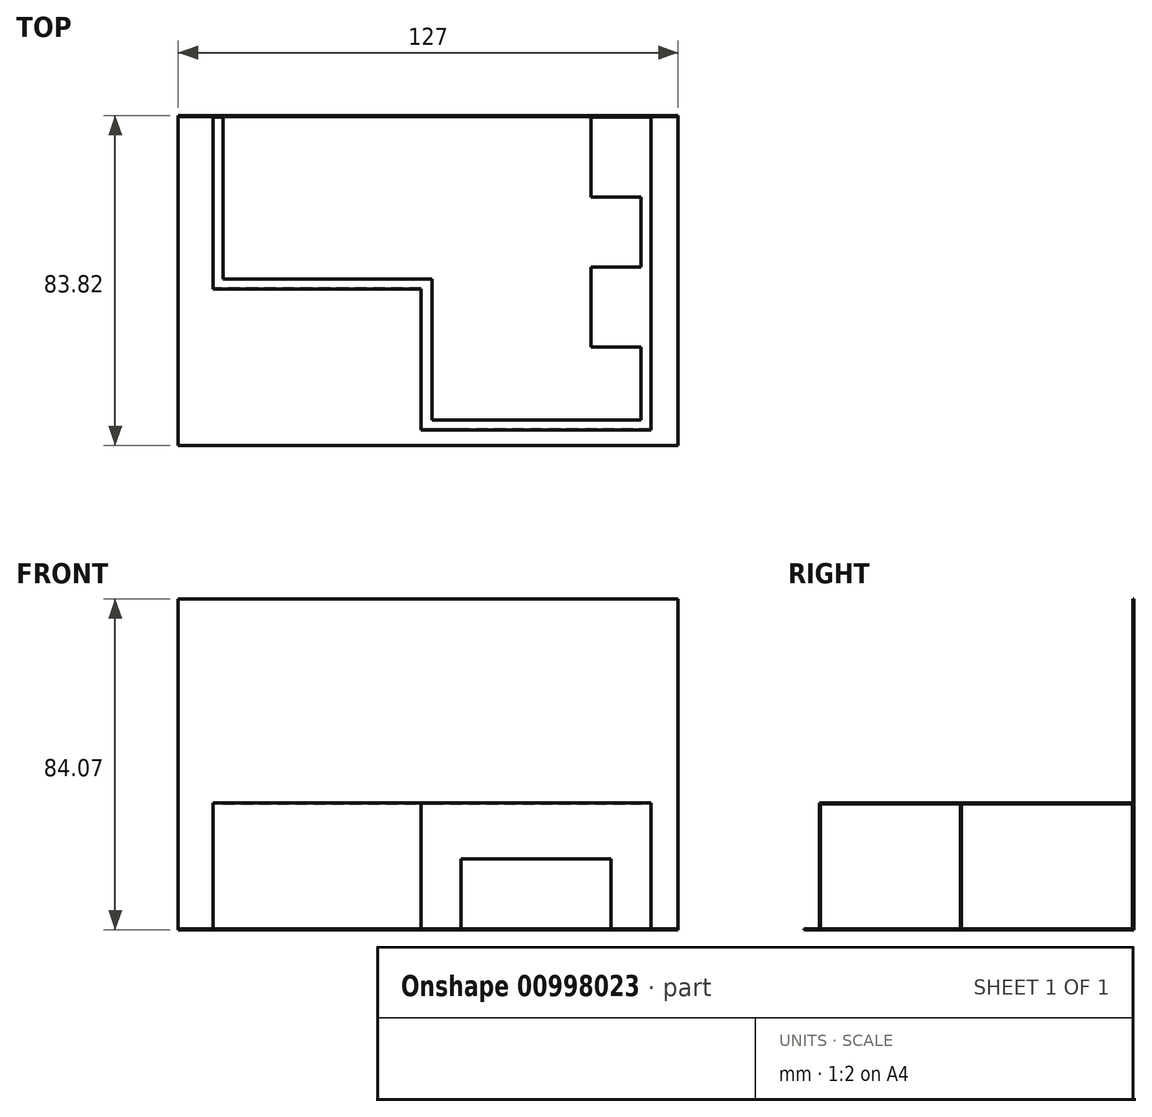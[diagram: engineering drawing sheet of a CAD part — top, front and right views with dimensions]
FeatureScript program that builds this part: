
annotation { "Feature Type Name" : "Feature", "Feature Type Description" : "" }
export const myFeature = defineFeature(function(context is Context, id is Id, definition is map)
    precondition{}
    {
        {
            var Q0;
            Q0=qCreatedBy(makeId("Top.planeOp"),FACE);
            var sketch = newSketch(context, id + "F0", { "sketchPlane" : qUnion([Q0])});
            skLineSegment(sketch, "E0.bottom", {"start": v(-60.1, 49.52) * mm, "end": v(66.9, 49.52) * mm});
            skLineSegment(sketch, "E0.top", {"start": v(-60.1, -34.3) * mm, "end": v(66.9, -34.3) * mm});
            skLineSegment(sketch, "E0.left", {"start": v(-60.1, 49.52) * mm, "end": v(-60.1, -34.3) * mm});
            skLineSegment(sketch, "E0.right", {"start": v(66.9, 49.52) * mm, "end": v(66.9, -34.3) * mm});
            skSolve(sketch);
        }
        {
            var Q0;
            Q0 = qSketchRegion(id + "F0", true);
            extrude(context, id + "F1", {"entities" : qUnion([Q0]), "depth" : 0.25 * mm, "offsetDistance" : 25.4 * mm});
        }
        {
            var Q0;
            Q0=makeQuery(id+"F1.opExtrude","CAP_FACE",FACE,{"disambiguationData":[OSD([sQuery(id+"F0.wireOp",EDGE,"E0.bottom"),sQuery(id+"F0.wireOp",EDGE,"E0.top"),sQuery(id+"F0.wireOp",EDGE,"E0.left"),sQuery(id+"F0.wireOp",EDGE,"E0.right")])],"isStart":false});
            var sketch = newSketch(context, id + "F2", { "sketchPlane" : qUnion([Q0])});
            skLineSegment(sketch, "E1.bottom", {"start": v(-60.1, 49.52) * mm, "end": v(66.9, 49.52) * mm});
            skLineSegment(sketch, "E1.top", {"start": v(-60.1, 49.26) * mm, "end": v(66.9, 49.26) * mm});
            skLineSegment(sketch, "E1.left", {"start": v(-60.1, 49.52) * mm, "end": v(-60.1, 49.26) * mm});
            skLineSegment(sketch, "E1.right", {"start": v(66.9, 49.52) * mm, "end": v(66.9, 49.26) * mm});
            skSolve(sketch);
        }
        {
            var Q0;
            Q0 = qSketchRegion(id + "F2", true);
            extrude(context, id + "F3", {"entities" : qUnion([Q0]), "operationType" : NewBodyOperationType.ADD, "depth" : 83.82 * mm, "offsetDistance" : 25.4 * mm});
        }
        {
            var Q0;
            Q0=makeQuery(id+"F1.opExtrude","CAP_FACE",FACE,{"disambiguationData":[OSD([sQuery(id+"F0.wireOp",EDGE,"E0.bottom"),sQuery(id+"F0.wireOp",EDGE,"E0.top"),sQuery(id+"F0.wireOp",EDGE,"E0.left"),sQuery(id+"F0.wireOp",EDGE,"E0.right")])],"isStart":false});
            var sketch = newSketch(context, id + "F4", { "sketchPlane" : qUnion([Q0])});
            skLineSegment(sketch, "E2.bottom", {"start": v(60, -30.39) * mm, "end": v(1.57, -30.39) * mm});
            skLineSegment(sketch, "E2.top", {"start": v(60, -30.13) * mm, "end": v(1.57, -30.13) * mm});
            skLineSegment(sketch, "E2.left", {"start": v(60, -30.39) * mm, "end": v(60, -30.13) * mm});
            skLineSegment(sketch, "E2.right", {"start": v(1.57, -30.39) * mm, "end": v(1.57, -30.13) * mm});
            skSolve(sketch);
        }
        {
            var Q0;
            Q0 = qSketchRegion(id + "F4", true);
            extrude(context, id + "F5", {"entities" : qUnion([Q0]), "operationType" : NewBodyOperationType.ADD, "depth" : 31.75 * mm, "offsetDistance" : 25.4 * mm});
        }
        {
            var Q0;
            Q0=makeQuery(id+"F5.opExtrude","CAP_FACE",FACE,{"disambiguationData":[OSD([sQuery(id+"F4.wireOp",EDGE,"E2.bottom"),sQuery(id+"F4.wireOp",EDGE,"E2.top"),sQuery(id+"F4.wireOp",EDGE,"E2.left"),sQuery(id+"F4.wireOp",EDGE,"E2.right")])],"isStart":false});
            var sketch = newSketch(context, id + "F6", { "sketchPlane" : qUnion([Q0])});
            skLineSegment(sketch, "E3.bottom", {"start": v(60, -30.39) * mm, "end": v(1.57, -30.39) * mm});
            skLineSegment(sketch, "E3.top", {"start": v(60, 49.12) * mm, "end": v(1.57, 49.12) * mm});
            skLineSegment(sketch, "E3.left", {"start": v(60, -30.39) * mm, "end": v(60, 49.12) * mm});
            skLineSegment(sketch, "E3.right", {"start": v(1.57, -30.39) * mm, "end": v(1.57, 49.12) * mm});
            skSolve(sketch);
        }
        {
            var Q0;
            Q0 = qSketchRegion(id + "F6", true);
            extrude(context, id + "F7", {"entities" : qUnion([Q0]), "operationType" : NewBodyOperationType.ADD, "depth" : 0.25 * mm, "offsetDistance" : 25.4 * mm});
        }
        {
            var Q0;
            Q0=makeQuery(id+"F7.boolean.opBoolean","MERGE",FACE,{"derivedFrom":[makeQuery(id+"F5.opExtrude","SWEPT_FACE",FACE,{"disambiguationData":[OSD([sQuery(id+"F4.wireOp",EDGE,"E2.right")])]}),makeQuery(id+"F7.opExtrude","SWEPT_FACE",FACE,{"disambiguationData":[OSD([sQuery(id+"F6.wireOp",EDGE,"E3.right")])]})]});
            var sketch = newSketch(context, id + "F8", { "sketchPlane" : qUnion([Q0])});
            skLineSegment(sketch, "E4.bottom", {"start": v(-5.48, 32) * mm, "end": v(-49.12, 32) * mm});
            skLineSegment(sketch, "E4.top", {"start": v(-5.48, 32.26) * mm, "end": v(-49.12, 32.26) * mm});
            skLineSegment(sketch, "E4.left", {"start": v(-5.48, 32) * mm, "end": v(-5.48, 32.26) * mm});
            skLineSegment(sketch, "E4.right", {"start": v(-49.12, 32) * mm, "end": v(-49.12, 32.26) * mm});
            skSolve(sketch);
        }
        {
            var Q0;
            Q0 = qSketchRegion(id + "F8", true);
            extrude(context, id + "F9", {"entities" : qUnion([Q0]), "operationType" : NewBodyOperationType.ADD, "depth" : 52.83 * mm, "offsetDistance" : 25.4 * mm});
        }
        {
            var Q0;
            Q0=makeQuery(id+"F9.boolean.opBoolean","MERGE",FACE,{"derivedFrom":[makeQuery(id+"F7.opExtrude","CAP_FACE",FACE,{"disambiguationData":[OSD([sQuery(id+"F6.wireOp",EDGE,"E3.bottom"),sQuery(id+"F6.wireOp",EDGE,"E3.top"),sQuery(id+"F6.wireOp",EDGE,"E3.left"),sQuery(id+"F6.wireOp",EDGE,"E3.right")])],"isStart":true}),makeQuery(id+"F9.opExtrude","SWEPT_FACE",FACE,{"disambiguationData":[OSD([sQuery(id+"F8.wireOp",EDGE,"E4.bottom")])]})]});
            var sketch = newSketch(context, id + "F10", { "sketchPlane" : qUnion([Q0])});
            skLineSegment(sketch, "E5.bottom", {"start": v(1.57, -5.48) * mm, "end": v(-51.26, -5.48) * mm});
            skLineSegment(sketch, "E5.top", {"start": v(1.57, -5.73) * mm, "end": v(-51.26, -5.73) * mm});
            skLineSegment(sketch, "E5.left", {"start": v(1.57, -5.48) * mm, "end": v(1.57, -5.73) * mm});
            skLineSegment(sketch, "E5.right", {"start": v(-51.26, -5.48) * mm, "end": v(-51.26, -5.73) * mm});
            skLineSegment(sketch, "E6.bottom", {"start": v(-51.26, -5.73) * mm, "end": v(-51, -5.73) * mm});
            skLineSegment(sketch, "E6.top", {"start": v(-51.26, -49.12) * mm, "end": v(-51, -49.12) * mm});
            skLineSegment(sketch, "E6.left", {"start": v(-51.26, -5.73) * mm, "end": v(-51.26, -49.12) * mm});
            skLineSegment(sketch, "E6.right", {"start": v(-51, -5.73) * mm, "end": v(-51, -49.12) * mm});
            skSolve(sketch);
        }
        {
            var Q0;
            Q0 = qSketchRegion(id + "F10", true);
            var Q1;
            Q1=makeQuery(id+"F1.opExtrude","CAP_FACE",FACE,{"disambiguationData":[OSD([sQuery(id+"F0.wireOp",EDGE,"E0.bottom"),sQuery(id+"F0.wireOp",EDGE,"E0.top"),sQuery(id+"F0.wireOp",EDGE,"E0.left"),sQuery(id+"F0.wireOp",EDGE,"E0.right")])],"isStart":false});
            extrude(context, id + "F11", {"entities" : qUnion([Q0]), "operationType" : NewBodyOperationType.ADD, "endBound" : BoundingType.UP_TO_SURFACE, "depth" : 25.4 * mm, "endBoundEntityFace" : qUnion([Q1]), "offsetDistance" : 25.4 * mm});
        }
        {
            var Q0;
            Q0=makeQuery(id+"F9.boolean.opBoolean","MERGE",FACE,{"derivedFrom":[makeQuery(id+"F7.opExtrude","CAP_FACE",FACE,{"disambiguationData":[OSD([sQuery(id+"F6.wireOp",EDGE,"E3.bottom"),sQuery(id+"F6.wireOp",EDGE,"E3.top"),sQuery(id+"F6.wireOp",EDGE,"E3.left"),sQuery(id+"F6.wireOp",EDGE,"E3.right")])],"isStart":false}),makeQuery(id+"F9.opExtrude","SWEPT_FACE",FACE,{"disambiguationData":[OSD([sQuery(id+"F8.wireOp",EDGE,"E4.top")])]})]});
            var sketch = newSketch(context, id + "F12", { "sketchPlane" : qUnion([Q0])});
            skLineSegment(sketch, "E7.bottom", {"start": v(-48.72, 8.02) * mm, "end": v(4.37, 8.02) * mm});
            skLineSegment(sketch, "E7.top", {"start": v(-48.72, 49.12) * mm, "end": v(57.45, 49.12) * mm});
            skLineSegment(sketch, "E7.left", {"start": v(-48.72, 8.02) * mm, "end": v(-48.72, 49.12) * mm});
            skLineSegment(sketch, "E7.right", {"start": v(57.45, 11.02) * mm, "end": v(57.45, 28.8) * mm});
            skLineSegment(sketch, "E8.top", {"start": v(4.37, -27.85) * mm, "end": v(57.45, -27.85) * mm});
            skLineSegment(sketch, "E8.left", {"start": v(4.37, 8.02) * mm, "end": v(4.37, -27.85) * mm});
            skLineSegment(sketch, "E8.right", {"start": v(57.45, -9.3) * mm, "end": v(57.45, -27.85) * mm});
            skLineSegment(sketch, "E9.bottom", {"start": v(57.45, 49.12) * mm, "end": v(44.75, 49.12) * mm});
            skLineSegment(sketch, "E9.top", {"start": v(57.45, 28.8) * mm, "end": v(44.75, 28.8) * mm});
            skLineSegment(sketch, "E9.right", {"start": v(44.75, 49.12) * mm, "end": v(44.75, 28.8) * mm});
            skLineSegment(sketch, "E10.bottom", {"start": v(57.45, 11.02) * mm, "end": v(44.75, 11.02) * mm});
            skLineSegment(sketch, "E10.top", {"start": v(57.45, -9.3) * mm, "end": v(44.75, -9.3) * mm});
            skLineSegment(sketch, "E10.right", {"start": v(44.75, 11.02) * mm, "end": v(44.75, -9.3) * mm});
            skPoint(sketch, "E11.orphan", {"position": v(57.45, 8.02) * mm});
            skSolve(sketch);
        }
        {
            var Q0;
            Q0 = qSketchRegion(id + "F12", true);
            extrude(context, id + "F13", {"entities" : qUnion([Q0]), "operationType" : NewBodyOperationType.REMOVE, "oppositeDirection" : true, "depth" : 5.33 * mm, "offsetDistance" : 25.4 * mm});
        }
        {
            var Q0;
            Q0=makeQuery(id+"F7.boolean.opBoolean","MERGE",FACE,{"derivedFrom":[makeQuery(id+"F5.opExtrude","SWEPT_FACE",FACE,{"disambiguationData":[OSD([sQuery(id+"F4.wireOp",EDGE,"E2.bottom")])]}),makeQuery(id+"F7.opExtrude","SWEPT_FACE",FACE,{"disambiguationData":[OSD([sQuery(id+"F6.wireOp",EDGE,"E3.bottom")])]})]});
            var sketch = newSketch(context, id + "F14", { "sketchPlane" : qUnion([Q0])});
            skLineSegment(sketch, "E12.bottom", {"start": v(11.73, 0.25) * mm, "end": v(49.83, 0.25) * mm});
            skLineSegment(sketch, "E12.top", {"start": v(11.73, 18.03) * mm, "end": v(49.83, 18.03) * mm});
            skLineSegment(sketch, "E12.left", {"start": v(11.73, 0.25) * mm, "end": v(11.73, 18.03) * mm});
            skLineSegment(sketch, "E12.right", {"start": v(49.83, 0.25) * mm, "end": v(49.83, 18.03) * mm});
            skSolve(sketch);
        }
        {
            var Q0;
            Q0 = qSketchRegion(id + "F14", true);
            extrude(context, id + "F15", {"entities" : qUnion([Q0]), "operationType" : NewBodyOperationType.REMOVE, "oppositeDirection" : true, "depth" : 25.4 * mm, "offsetDistance" : 25.4 * mm});
        }
    });
